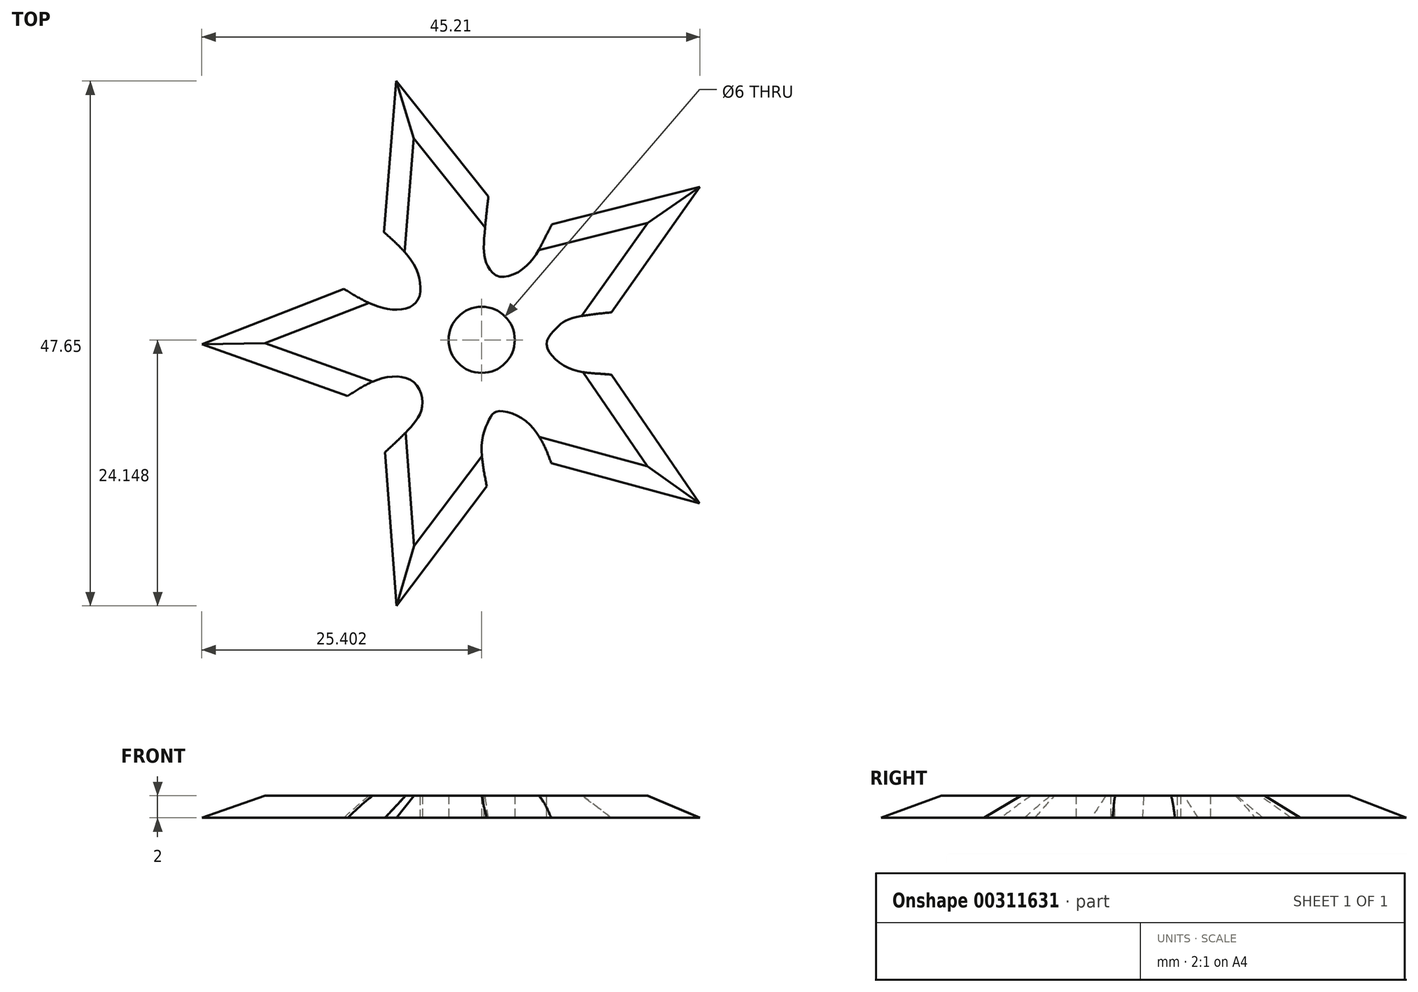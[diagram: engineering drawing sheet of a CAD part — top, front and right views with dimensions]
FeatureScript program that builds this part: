
annotation { "Feature Type Name" : "Feature", "Feature Type Description" : "" }
export const myFeature = defineFeature(function(context is Context, id is Id, definition is map)
    precondition{}
    {
        {
            var Q0;
            Q0=qCreatedBy(makeId("Top.planeOp"),FACE);
            var sketch = newSketch(context, id + "F0", { "sketchPlane" : qUnion([Q0])});
            skLineSegment(sketch, "E0", {"start": v(-7.17, 9.2) * mm, "end": v(-6.07, 22.95) * mm});
            skLineSegment(sketch, "E1", {"start": v(-6.07, 22.95) * mm, "end": v(2.3, 12.5) * mm});
            skLineSegment(sketch, "E2", {"start": v(8.07, 9.95) * mm, "end": v(21.5, 13.33) * mm});
            skLineSegment(sketch, "E3", {"start": v(21.5, 13.33) * mm, "end": v(13.45, 1.95) * mm});
            skLineSegment(sketch, "E4", {"start": v(13.45, -3.7) * mm, "end": v(21.44, -15.38) * mm});
            skLineSegment(sketch, "E5", {"start": v(21.44, -15.38) * mm, "end": v(7.99, -11.73) * mm});
            skLineSegment(sketch, "E6", {"start": v(2.15, -13.84) * mm, "end": v(-6.04, -24.7) * mm});
            skLineSegment(sketch, "E7", {"start": v(-6.04, -24.7) * mm, "end": v(-7.09, -10.76) * mm});
            skLineSegment(sketch, "E8", {"start": v(-10.5, -5.65) * mm, "end": v(-23.7, -0.95) * mm});
            skLineSegment(sketch, "E9", {"start": v(-23.7, -0.95) * mm, "end": v(-10.82, 4.07) * mm});
            skFitSpline(sketch, "E10", {"points": [v(-10.82, 4.07) * mm, v(-7, 2.29) * mm, v(-4.25, 2.86) * mm, v(-4.25, 5.86) * mm, v(-7.17, 9.2) * mm], "startDerivative": vector(13.76, -8.43) * mm, "endDerivative": vector(-12.57, 11.06) * mm});
            skFitSpline(sketch, "E11", {"points": [v(2.3, 12.5) * mm, v(1.9, 8.28) * mm, v(2.08, 6.5) * mm, v(3.27, 5.2) * mm, v(5.78, 6.18) * mm, v(7.21, 8.29) * mm, v(8.07, 9.95) * mm], "startDerivative": vector(-2.37, -21.22) * mm, "endDerivative": vector(5.72, 10.91) * mm});
            skFitSpline(sketch, "E12", {"points": [v(13.45, 1.95) * mm, v(9.59, 1.31) * mm, v(8.52, 0.56) * mm, v(7.58, -0.98) * mm, v(9.56, -3.09) * mm, v(12.3, -3.62) * mm, v(13.45, -3.7) * mm], "startDerivative": vector(-20.55, -2.16) * mm, "endDerivative": vector(8.57, -0.75) * mm});
            skFitSpline(sketch, "E13", {"points": [v(2.15, -13.84) * mm, v(1.72, -9.7) * mm, v(2.45, -7.64) * mm, v(3.08, -7.05) * mm, v(5.46, -7.75) * mm, v(7.39, -10.22) * mm, v(7.99, -11.73) * mm], "startDerivative": vector(-3.91, 19.62) * mm, "endDerivative": vector(3.38, -9.94) * mm});
            skFitSpline(sketch, "E14", {"points": [v(-10.5, -5.65) * mm, v(-7.38, -4.05) * mm, v(-4.59, -4.32) * mm, v(-3.7, -6.5) * mm, v(-4.6, -8.3) * mm, v(-5.92, -9.66) * mm, v(-7.09, -10.76) * mm], "startDerivative": vector(14.65, 9.52) * mm, "endDerivative": vector(-8.3, -7.74) * mm});
            skSolve(sketch);
        }
        {
            var Q0;
            Q0=makeQuery(id+"F0.imprint","IMPRINT",FACE,{"disambiguationData":[TD([[makeQuery(id+"F0.imprint","IMPRINT",EDGE,{"derivedFrom":sQuery(id+"F0.wireOp",EDGE,"E0")}),-1.0]])]});
            extrude(context, id + "F1", {"entities" : qUnion([Q0]), "depth" : 2 * mm});
        }
        {
            var Q0;
            Q0=makeQuery(id+"F1.opExtrude","CAP_EDGE",EDGE,{"disambiguationData":[OSD([sQuery(id+"F0.wireOp",EDGE,"E1")])],"isStart":false});
            var Q1;
            Q1=makeQuery(id+"F1.opExtrude","CAP_EDGE",EDGE,{"disambiguationData":[OSD([sQuery(id+"F0.wireOp",EDGE,"E0")])],"isStart":false});
            var Q2;
            Q2=makeQuery(id+"F1.opExtrude","CAP_EDGE",EDGE,{"disambiguationData":[OSD([sQuery(id+"F0.wireOp",EDGE,"E3")])],"isStart":false});
            var Q3;
            Q3=makeQuery(id+"F1.opExtrude","CAP_EDGE",EDGE,{"disambiguationData":[OSD([sQuery(id+"F0.wireOp",EDGE,"E2")])],"isStart":false});
            var Q4;
            Q4=makeQuery(id+"F1.opExtrude","CAP_EDGE",EDGE,{"disambiguationData":[OSD([sQuery(id+"F0.wireOp",EDGE,"E4")])],"isStart":false});
            var Q5;
            Q5=makeQuery(id+"F1.opExtrude","CAP_EDGE",EDGE,{"disambiguationData":[OSD([sQuery(id+"F0.wireOp",EDGE,"E5")])],"isStart":false});
            var Q6;
            Q6=makeQuery(id+"F1.opExtrude","CAP_EDGE",EDGE,{"disambiguationData":[OSD([sQuery(id+"F0.wireOp",EDGE,"E6")])],"isStart":false});
            var Q7;
            Q7=makeQuery(id+"F1.opExtrude","CAP_EDGE",EDGE,{"disambiguationData":[OSD([sQuery(id+"F0.wireOp",EDGE,"E7")])],"isStart":false});
            var Q8;
            Q8=makeQuery(id+"F1.opExtrude","CAP_EDGE",EDGE,{"disambiguationData":[OSD([sQuery(id+"F0.wireOp",EDGE,"E8")])],"isStart":false});
            var Q9;
            Q9=makeQuery(id+"F1.opExtrude","CAP_EDGE",EDGE,{"disambiguationData":[OSD([sQuery(id+"F0.wireOp",EDGE,"E9")])],"isStart":false});
            chamfer(context, id + "F2", {"entities" : qUnion([Q0, Q1, Q2, Q3, Q4, Q5, Q6, Q7, Q8, Q9]), "width" : 2 * mm, "tangentPropagation" : true});
        }
        {
            var Q0;
            Q0=qCreatedBy(makeId("Top.planeOp"),FACE);
            var sketch = newSketch(context, id + "F3", { "sketchPlane" : qUnion([Q0])});
            skLineSegment(sketch, "E15", {"start": v(22.8, -16.31) * mm, "end": v(-8.5, 6.69) * mm, "construction": true});
            skLineSegment(sketch, "E16", {"start": v(22.92, 14.14) * mm, "end": v(-8.9, -7.88) * mm, "construction": true});
            skLineSegment(sketch, "E17", {"start": v(-6.32, 24.33) * mm, "end": v(5.27, -11.67) * mm, "construction": true});
            skLineSegment(sketch, "E18", {"start": v(1.7, -0.55) * mm, "end": v(4.01, 1.86) * mm});
            skLineSegment(sketch, "E19", {"start": v(4.01, 1.86) * mm, "end": v(-0.43, -2.75) * mm});
            skSolve(sketch);
        }
        {
            var Q0;
            Q0=sQuery(id+"F3.wireOp",VERTEX,"E18.start");
            var Q1;
            Q1=makeQuery(id+"F1.opExtrude","SWEPT_BODY",BODY,{"disambiguationData":[OSD([sQuery(id+"F0.wireOp",EDGE,"E0"),sQuery(id+"F0.wireOp",EDGE,"E1"),sQuery(id+"F0.wireOp",EDGE,"E2"),sQuery(id+"F0.wireOp",EDGE,"E3"),sQuery(id+"F0.wireOp",EDGE,"E4"),sQuery(id+"F0.wireOp",EDGE,"E5"),sQuery(id+"F0.wireOp",EDGE,"E6"),sQuery(id+"F0.wireOp",EDGE,"E7"),sQuery(id+"F0.wireOp",EDGE,"E8"),sQuery(id+"F0.wireOp",EDGE,"E9"),sQuery(id+"F0.wireOp",EDGE,"E10"),sQuery(id+"F0.wireOp",EDGE,"E11"),sQuery(id+"F0.wireOp",EDGE,"E12"),sQuery(id+"F0.wireOp",EDGE,"E13"),sQuery(id+"F0.wireOp",EDGE,"E14")])]});
            hole(context, id + "F4", {"style" : HoleStyle.SIMPLE, "endStyle" : HoleEndStyle.THROUGH, "oppositeDirection" : true, "holeDiameter" : 6 * mm, "tappedDepth" : 12 * mm, "tapClearance" : 3, "locations" : qUnion([Q0]), "scope" : qUnion([Q1])});
        }
    });
